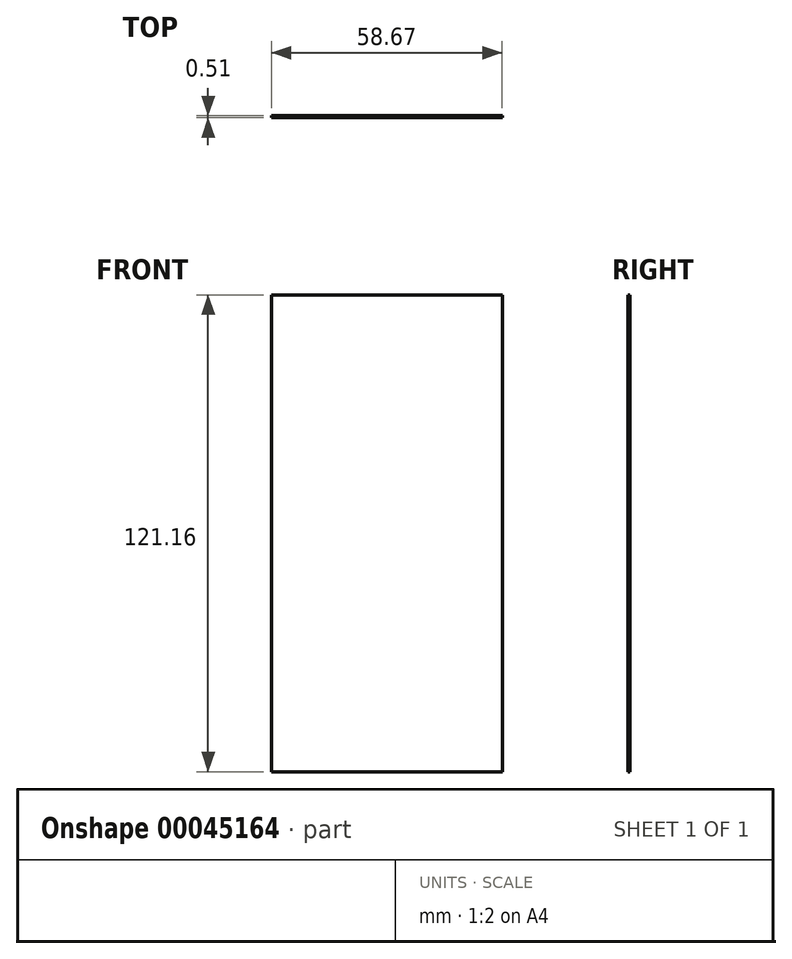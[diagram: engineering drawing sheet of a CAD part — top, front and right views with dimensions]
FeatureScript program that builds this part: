
annotation { "Feature Type Name" : "Feature", "Feature Type Description" : "" }
export const myFeature = defineFeature(function(context is Context, id is Id, definition is map)
    precondition{}
    {
        {
            var Q0;
            Q0=qCreatedBy(makeId("Front.planeOp"),FACE);
            var sketch = newSketch(context, id + "F0", { "sketchPlane" : qUnion([Q0])});
            skLineSegment(sketch, "E0", {"start": v(0, 0) * mm, "end": v(58.67, 0) * mm});
            skLineSegment(sketch, "E1", {"start": v(58.67, 0) * mm, "end": v(58.67, 121.16) * mm});
            skLineSegment(sketch, "E2", {"start": v(58.67, 121.16) * mm, "end": v(0, 121.16) * mm});
            skLineSegment(sketch, "E3", {"start": v(0, 121.16) * mm, "end": v(0, 0) * mm});
            skLineSegment(sketch, "E4", {"start": v(0, 0) * mm, "end": v(2.54, 0) * mm});
            skLineSegment(sketch, "E5", {"start": v(2.54, 0) * mm, "end": v(2.54, 2.54) * mm});
            skLineSegment(sketch, "E6", {"start": v(2.54, 2.54) * mm, "end": v(0, 2.54) * mm});
            skLineSegment(sketch, "E7", {"start": v(56.13, 0) * mm, "end": v(56.13, 2.54) * mm});
            skLineSegment(sketch, "E8", {"start": v(56.13, 2.54) * mm, "end": v(58.67, 2.54) * mm});
            skLineSegment(sketch, "E9", {"start": v(0, 121.16) * mm, "end": v(0, 118.62) * mm});
            skLineSegment(sketch, "E10", {"start": v(0, 118.62) * mm, "end": v(2.54, 118.62) * mm});
            skLineSegment(sketch, "E11", {"start": v(2.54, 118.62) * mm, "end": v(2.54, 121.16) * mm});
            skLineSegment(sketch, "E12", {"start": v(58.67, 121.16) * mm, "end": v(58.67, 118.62) * mm});
            skLineSegment(sketch, "E13", {"start": v(58.67, 118.62) * mm, "end": v(56.13, 118.62) * mm});
            skLineSegment(sketch, "E14", {"start": v(56.13, 118.62) * mm, "end": v(56.13, 121.16) * mm});
            skLineSegment(sketch, "E15", {"start": v(2.54, 2.54) * mm, "end": v(2.54, 118.62) * mm, "construction": true});
            skLineSegment(sketch, "E16", {"start": v(2.54, 118.62) * mm, "end": v(56.13, 118.62) * mm, "construction": true});
            skLineSegment(sketch, "E17", {"start": v(56.13, 118.62) * mm, "end": v(56.13, 2.54) * mm, "construction": true});
            skLineSegment(sketch, "E18", {"start": v(56.13, 2.54) * mm, "end": v(2.54, 2.54) * mm, "construction": true});
            skSolve(sketch);
        }
        {
            var Q0;
            Q0=qSketchRegion(id+"F0",true);
            extrude(context, id + "F1", {"entities" : qUnion([Q0]), "depth" : 0.5 * mm});
        }
    });
